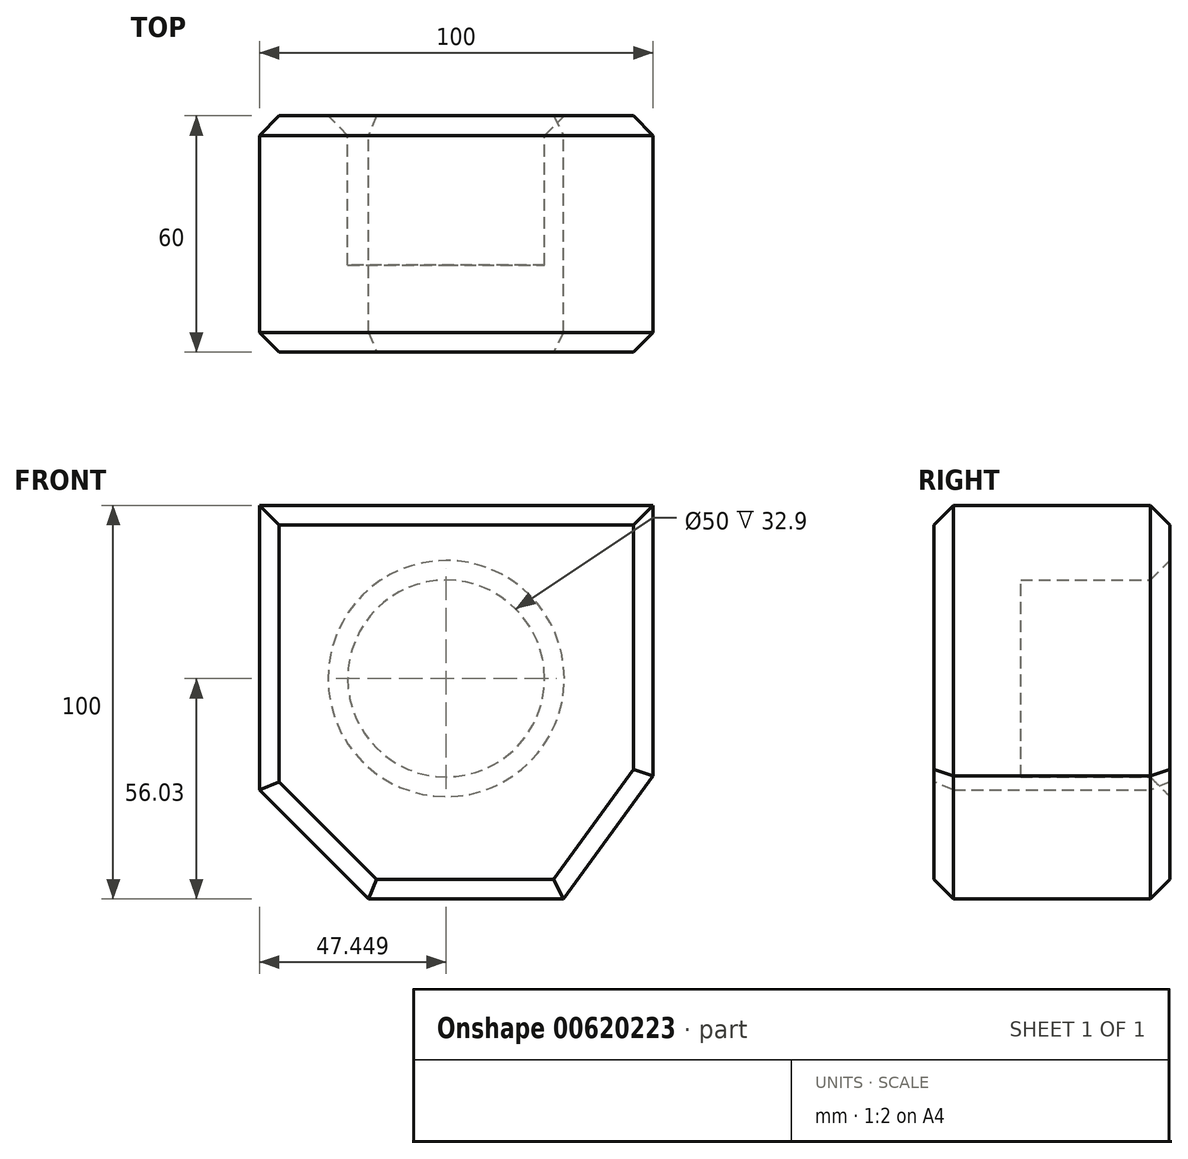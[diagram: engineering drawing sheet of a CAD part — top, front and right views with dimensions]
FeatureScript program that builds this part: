
annotation { "Feature Type Name" : "Feature", "Feature Type Description" : "" }
export const myFeature = defineFeature(function(context is Context, id is Id, definition is map)
    precondition{}
    {
        {
            var Q0;
            Q0=qCreatedBy(makeId("Front.planeOp"),FACE);
            var sketch = newSketch(context, id + "F0", { "sketchPlane" : qUnion([Q0])});
            skLineSegment(sketch, "E0.bottom", {"start": v(-58.2, 43.97) * mm, "end": v(41.8, 43.97) * mm});
            skLineSegment(sketch, "E0.top", {"start": v(-30.49, -56.03) * mm, "end": v(19.07, -56.03) * mm});
            skLineSegment(sketch, "E0.left", {"start": v(-58.2, 43.97) * mm, "end": v(-58.2, -28.32) * mm});
            skLineSegment(sketch, "E0.right", {"start": v(41.8, 43.97) * mm, "end": v(41.8, -24.68) * mm});
            skPoint(sketch, "E1.orphan", {"position": v(19.64, -66.15) * mm});
            skPoint(sketch, "E2.orphan", {"position": v(-35.55, -66.15) * mm});
            skLineSegment(sketch, "E3", {"start": v(41.8, -24.68) * mm, "end": v(19.07, -56.03) * mm});
            skLineSegment(sketch, "E4", {"start": v(-58.2, -28.32) * mm, "end": v(-30.49, -56.03) * mm});
            skPoint(sketch, "E5.orphan", {"position": v(13.13, -64.22) * mm});
            skPoint(sketch, "E6.orphan", {"position": v(-22.3, -64.22) * mm});
            skSolve(sketch);
        }
        {
            var Q0;
            Q0 = qSketchRegion(id + "F0", true);
            extrude(context, id + "F1", {"entities" : qUnion([Q0]), "depth" : 60 * mm, "offsetDistance" : 25 * mm});
        }
        {
            var Q0;
            Q0=makeQuery(id+"F1.opExtrude","CAP_FACE",FACE,{"disambiguationData":[OSD([sQuery(id+"F0.wireOp",EDGE,"E0.bottom"),sQuery(id+"F0.wireOp",EDGE,"E0.top"),sQuery(id+"F0.wireOp",EDGE,"E0.left"),sQuery(id+"F0.wireOp",EDGE,"E0.right"),sQuery(id+"F0.wireOp",EDGE,"E3"),sQuery(id+"F0.wireOp",EDGE,"E4")])],"isStart":false});
            chamfer(context, id + "F2", {"entities" : qUnion([Q0]), "width" : 5 * mm, "tangentPropagation" : true});
        }
        {
            var Q0;
            Q0=qCreatedBy(makeId("Front.planeOp"),FACE);
            var sketch = newSketch(context, id + "F3", { "sketchPlane" : qUnion([Q0])});
            skCircle(sketch, "E7", {"center": v(-10.75, 0) * mm, "radius": 25 * mm});
            skSolve(sketch);
        }
        {
            var Q0;
            Q0 = qSketchRegion(id + "F3", true);
            extrude(context, id + "F4", {"entities" : qUnion([Q0]), "operationType" : NewBodyOperationType.REMOVE, "oppositeDirection" : true, "depth" : 25 * mm, "offsetDistance" : 25 * mm});
        }
        {
            var Q0;
            Q0 = qSketchRegion(id + "F3", true);
            extrude(context, id + "F5", {"entities" : qUnion([Q0]), "operationType" : NewBodyOperationType.REMOVE, "oppositeDirection" : true, "depth" : 25 * mm, "offsetDistance" : 25 * mm});
        }
        {
            var Q0;
            Q0 = qSketchRegion(id + "F3", true);
            extrude(context, id + "F6", {"entities" : qUnion([Q0]), "operationType" : NewBodyOperationType.REMOVE, "depth" : 37.9 * mm, "offsetDistance" : 25 * mm});
        }
        {
            var Q0;
            Q0=makeQuery(id+"F1.opExtrude","CAP_FACE",FACE,{"disambiguationData":[OSD([sQuery(id+"F0.wireOp",EDGE,"E0.bottom"),sQuery(id+"F0.wireOp",EDGE,"E0.top"),sQuery(id+"F0.wireOp",EDGE,"E0.left"),sQuery(id+"F0.wireOp",EDGE,"E0.right"),sQuery(id+"F0.wireOp",EDGE,"E3"),sQuery(id+"F0.wireOp",EDGE,"E4")])],"isStart":true});
            chamfer(context, id + "F7", {"entities" : qUnion([Q0]), "width" : 5 * mm, "tangentPropagation" : true});
        }
    });
